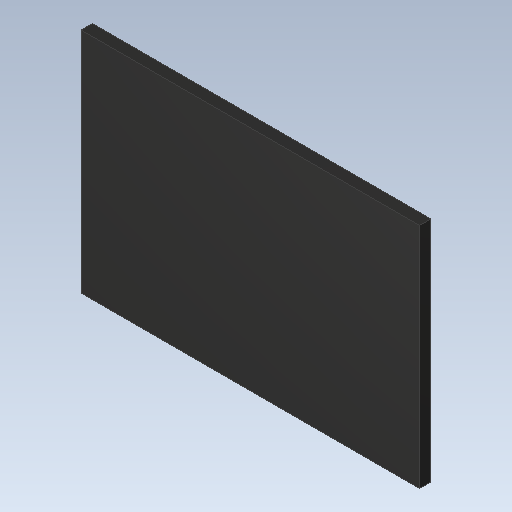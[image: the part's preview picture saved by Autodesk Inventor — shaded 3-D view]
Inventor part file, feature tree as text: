
AUTODESK INVENTOR PART (.ipt)
format: ipt  version: 2023 (Build 270158000, 158)  size: 92,160 bytes
history: imported  units: in
note: dims shown in document units (in); Inventor stores cm internally (conversion verified against a paired STEP export)
features: imported_body x1
ambient origin geometry x8: Origin, YZ Plane, XZ Plane, XY Plane, X Axis, Y Axis, Z Axis, Center Point
bodies: Solid1 (imported_parasolid), Body1 (imported_parasolid)
feature tree (1):
  imported_body  NMx_Import_Brep_tag  [imported B-rep: ~6 faces, bbox_mm=[2.9968, 2.0168, 0.1]]
